# Revit family: P6-SM Pendant Loudspeaker
name_source: partatom
category: Communication Devices
revit_build: Autodesk Revit 2017 (Build: 20190507_1515(x64)
units: mm (PartAtom-declared; Revit-internal decimal feet)

## family parameters
Always vertical = Yes
Cut with Voids When Loaded = No
Maintain Annotation Orientation = No
Part Type = Normal
Room Calculation Point = No
Round Connector Dimension = Use Diameter
Shared = No
Work Plane-Based = No

## types (1)
- P6-SM
    Accessories (included) = Two Griplock cbale fasteners
    Accessories (optional) = MC-SK10 inline splice kits
    Compliance = ETL listed to comply with UL std 1480A, 

Suspension system and Gripple cable fasteners listed per
UL1598 and UL2239, TUV and CSA Class 3426-01 and Class
3426-81.
    Continuous Power Handling @ Nominal Impedance = Passive / 19V / 60W @6 ohms (240W peak)
    Controls = Wattage / low impedance selector switch
    Description = Default
    Dimensions H x W (diameter) = 139 mm x 292mm (5.5" x 11.5")
    Finish = PC/ABS V-O plastic, matte finish (Black or White)
    Grille = Powder-coated perforated steel
White (RAL 9011) or Black (RAL 9010) finish
    Input Connection = Pre-terminated inside housing
    Manufacturer = Biamp
    Model = P6-SM
    Mounting Provisions = Two pre-terminated aircarft cables (one as primary support, one as a saftey cable), and Griplock cable fasteners. 14 feet (4.3 m) of pre-terminated Magic Cable
    Nominal Beamwidth (H x V) = 90°, conical
    Nominal Maximum SPL @ 1m = Passive / Peak - 111 db / Continuous - 105 dB
    Nominal Sensitivity @ 1m = Passive / @1W - 87 dB / @2.83V - 88 dB
    Operating Environment = Indoor/Outdoor (splash applications only)
    Operating Mode = Passive with DSP
    Operating Range = 75 Hz to 18.5 kHz (-10dB)
    Recommended Amplifiers = 60W - 102W @ 6 ohms, (19V - 27V)
    Required Accessories = 80 Hz, 12db/Oct High Pass
    Transducers = LF1 x 6.5" (165mm) polypropylene cone / HF1 x 1" (25mm) soft dome
    Transformer - 100V = 60W, 30W, 15W, 7.5W, 3.75W
    Transformer - 70V = 60W, 30W, 15W, 7.5W, 3.75W, 1.875W
    Type Comments = Not Used
    URL = Default
    Unit Weight = 5 kg (11 lbs)

## geometry (parser evidence)
native form markers: Blend x4, Sweep x2
no freeform markers — native parametric forms only
